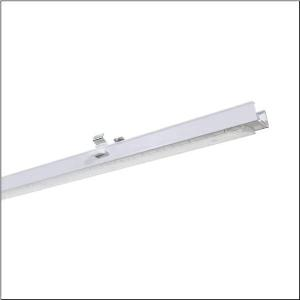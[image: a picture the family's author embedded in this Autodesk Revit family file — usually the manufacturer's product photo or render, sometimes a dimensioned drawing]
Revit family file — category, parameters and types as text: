
# Revit family: trunking_flex_31_51re12db4cb
name_source: partatom
category: Lighting Fixtures
units: mm (PartAtom-declared; Revit-internal decimal feet)

## family parameters
Cut with Voids When Loaded = No
Host = Face
Light Source = No
Part Type = Normal
Room Calculation Point = No
Round Connector Dimension = Use Diameter
Shared = No

## types (1)
- Trunking Flex 31 (1 x LED, 11500 lm, 66 W, 4000K)
    Apparent Load = 66 VA
    CIE Flux Codes = 65 91 98 99 100
    Color Rendering = 80
    Color Temperature = 4000K
    Default Elevation = 1800 mm
    Description = Trunking Flex 31, luminaire insert, of extruded aluminium section, coated, traffic white (RAL 9016), length: 1.472mm, width: 91mm, height: 53mm, LED rated luminous flux: 11.500lm, light colour: 840, control gear: DALI 2, with system connector: socket, mains connection: 220..240V, AC, 50/60Hz, rated input power: 66W, primary light control with lens, of plastic, primary optical cover: cover, of PMMA, light emission: direct distribution, protection rating (complete): IP20, insulation class (complete): insulation class I (protective earthing), certification: CE, UKCA, impact resistance: IK02, permissible ambient temperature for indoor applications: -20..+40°C, packaging unit: 1 piece
    Height = 58 mm
    Lamp = 1 x LED
    Lamp Light Flux = 11500 lm
    Lamp Power = 66 W
    Lamp count = 1
    Length = 1472 mm
    Luminous efficacy = 174 lm/W
    Manufacturer = Siteco
    ModVariant = No
    Model = 51RE12DB4CB
    Mounting Place = Ceiling
    Mounting Type = Pendant
    Number of Poles = 1
    OnlyDefault = Yes
    Power Factor = 1
    Product Name = Trunking Flex 31
    Product group = luminaire insert
    ProductGroupID = 901
    Protection Class = Protection class I
    Protection Degree = IP 20
    RLX_Detail_Level = 1
    RLX_Emergency_Light_Flux = 0 lm
    RLX_Emergency_Type = 0
    RLX_Emergency_Type_DB = No
    RlxData = <blob elided: 19541 chars, md5=92b84e75>
    Socket = socket
    Standby Power = 0 W
    System Light Flux = 11500 lm
    System Power = 66 W
    Type Comments = Product without accessories
    Type Image = l_1266702.jpg
    URL = http://relux.com
    VarID = ---
    Voltage = 0 V
    Weight = 0.00 kg
    Width = 65 mm

## geometry (parser evidence)
native form markers: Blend x4, Sweep x9
no freeform markers — native parametric forms only
